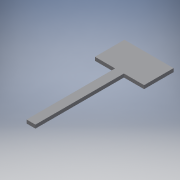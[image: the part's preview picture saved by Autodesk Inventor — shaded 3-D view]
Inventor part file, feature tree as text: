
AUTODESK INVENTOR PART (.ipt)
format: ipt  version: 2018.3 (Build 223284000, 284)  size: 92,672 bytes
history: native  units: mm
features: extrude x1, sketch x1
ambient origin geometry x8: Origin, YZ Plane, XZ Plane, XY Plane, X Axis, Y Axis, Z Axis, Center Point
bodies: Solid1 (feature_tree)
feature tree (2):
  extrude  "Extrusion1"  Depth=18.0mm
  sketch  "Sketch1"  dims[d0=1.8mm d1=18.0mm d2=10.0mm d3=6.0mm d4=4.1mm d5=4.1mm d6=0.7mm d7=0.0mm]
